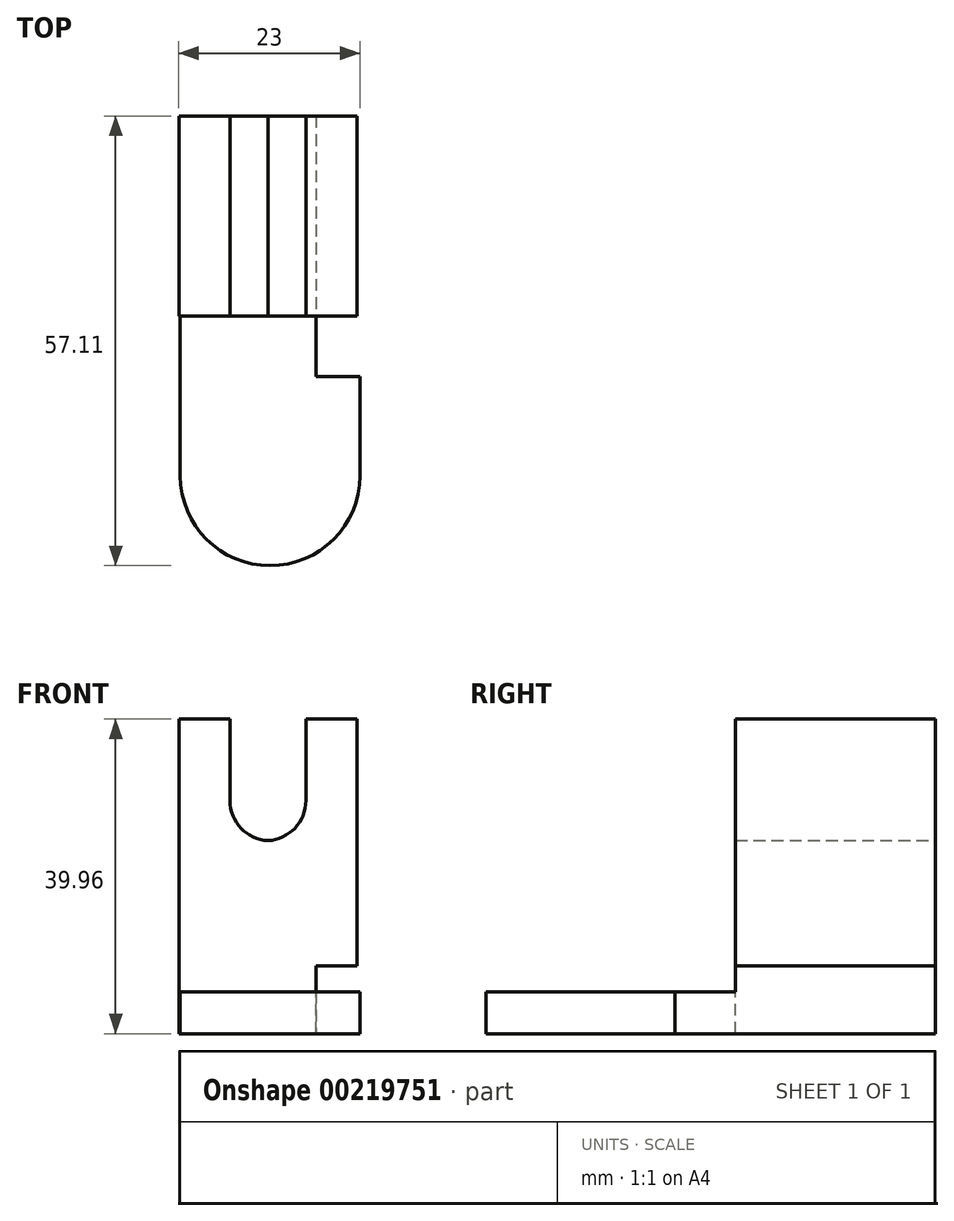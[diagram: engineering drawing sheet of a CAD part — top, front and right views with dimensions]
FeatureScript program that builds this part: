
annotation { "Feature Type Name" : "Feature", "Feature Type Description" : "" }
export const myFeature = defineFeature(function(context is Context, id is Id, definition is map)
    precondition{}
    {
        {
            var Q0;
            Q0=qCreatedBy(makeId("Front.planeOp"),FACE);
            var sketch = newSketch(context, id + "F0", { "sketchPlane" : qUnion([Q0])});
            skLineSegment(sketch, "E0.bottom", {"start": v(-11.13, 0) * mm, "end": v(11.5, 0) * mm});
            skLineSegment(sketch, "E0.top", {"start": v(-11.13, 39.96) * mm, "end": v(11.5, 39.96) * mm});
            skLineSegment(sketch, "E0.left", {"start": v(-11.13, 0) * mm, "end": v(-11.13, 39.96) * mm});
            skLineSegment(sketch, "E0.right", {"start": v(11.5, 0) * mm, "end": v(11.5, 39.96) * mm});
            skSolve(sketch);
        }
        {
            var Q0;
            Q0 = qSketchRegion(id + "F0", true);
            extrude(context, id + "F1", {"entities" : qUnion([Q0]), "depth" : 25.4 * mm});
        }
        {
            var Q0;
            Q0=makeQuery(id+"F1.opExtrude","CAP_FACE",FACE,{"disambiguationData":[OSD([sQuery(id+"F0.wireOp",EDGE,"E0.bottom"),sQuery(id+"F0.wireOp",EDGE,"E0.top"),sQuery(id+"F0.wireOp",EDGE,"E0.left"),sQuery(id+"F0.wireOp",EDGE,"E0.right")])],"isStart":false});
            var sketch = newSketch(context, id + "F2", { "sketchPlane" : qUnion([Q0])});
            skLineSegment(sketch, "E1.bottom", {"start": v(-4.64, 39.96) * mm, "end": v(5, 39.96) * mm});
            skLineSegment(sketch, "E1.top", {"start": v(-4.64, 24.52) * mm, "end": v(5, 24.52) * mm});
            skLineSegment(sketch, "E1.left", {"start": v(-4.64, 39.96) * mm, "end": v(-4.64, 24.52) * mm});
            skLineSegment(sketch, "E1.right", {"start": v(5, 39.96) * mm, "end": v(5, 24.52) * mm});
            skSolve(sketch);
        }
        {
            var Q0;
            Q0 = qSketchRegion(id + "F2", true);
            extrude(context, id + "F3", {"entities" : qUnion([Q0]), "operationType" : NewBodyOperationType.REMOVE, "endBound" : BoundingType.THROUGH_ALL, "oppositeDirection" : true, "depth" : 25.4 * mm});
        }
        {
            var Q0;
            Q0=makeQuery(id+"F3.boolean.opBoolean","COPY",EDGE,{"derivedFrom":makeQuery(id+"F3.opExtrude","SWEPT_EDGE",EDGE,{"disambiguationData":[OSD([sQuery(id+"F2.wireOp",EDGE,"E1.top"),sQuery(id+"F2.wireOp",EDGE,"E1.left")])]})});
            var Q1;
            Q1=makeQuery(id+"F3.boolean.opBoolean","COPY",EDGE,{"derivedFrom":makeQuery(id+"F3.opExtrude","SWEPT_EDGE",EDGE,{"disambiguationData":[OSD([sQuery(id+"F2.wireOp",EDGE,"E1.top"),sQuery(id+"F2.wireOp",EDGE,"E1.right")])]})});
            fillet(context, id + "F4", {"entities" : qUnion([Q0, Q1]), "radius" : 5.08 * mm, "tangentPropagation" : true, "allowEdgeOverflow" : false});
        }
        {
            var Q0;
            Q0=makeQuery(id+"F1.opExtrude","CAP_FACE",FACE,{"disambiguationData":[OSD([sQuery(id+"F0.wireOp",EDGE,"E0.bottom"),sQuery(id+"F0.wireOp",EDGE,"E0.top"),sQuery(id+"F0.wireOp",EDGE,"E0.left"),sQuery(id+"F0.wireOp",EDGE,"E0.right")])],"isStart":false});
            var sketch = newSketch(context, id + "F5", { "sketchPlane" : qUnion([Q0])});
            skLineSegment(sketch, "E2.bottom", {"start": v(11.5, 0) * mm, "end": v(6.3, 0) * mm});
            skLineSegment(sketch, "E2.top", {"start": v(11.5, 8.62) * mm, "end": v(6.3, 8.62) * mm});
            skLineSegment(sketch, "E2.left", {"start": v(11.5, 0) * mm, "end": v(11.5, 8.62) * mm});
            skLineSegment(sketch, "E2.right", {"start": v(6.3, 0) * mm, "end": v(6.3, 8.62) * mm});
            skSolve(sketch);
        }
        {
            var Q0;
            Q0=makeQuery(id+"F5.imprint","IMPRINT",FACE,{"disambiguationData":[TD([[makeQuery(id+"F5.imprint","IMPRINT",EDGE,{"derivedFrom":sQuery(id+"F5.wireOp",EDGE,"E2.bottom")}),1.0]])]});
            extrude(context, id + "F6", {"entities" : qUnion([Q0]), "operationType" : NewBodyOperationType.REMOVE, "endBound" : BoundingType.THROUGH_ALL, "oppositeDirection" : true, "depth" : 25.4 * mm});
        }
        {
            var Q0;
            Q0=qCreatedBy(makeId("Top.planeOp"),FACE);
            var sketch = newSketch(context, id + "F7", { "sketchPlane" : qUnion([Q0])});
            skLineSegment(sketch, "E3.bottom", {"start": v(-10.94, 0) * mm, "end": v(6.3, 0) * mm});
            skLineSegment(sketch, "E3.left", {"start": v(-10.94, 0) * mm, "end": v(-10.94, -45.7) * mm});
            skLineSegment(sketch, "E3.right", {"start": v(11.87, -33.1) * mm, "end": v(11.87, -45.7) * mm});
            skLineSegment(sketch, "E4.0", {"start": v(6.3, 0) * mm, "end": v(6.3, -25.4) * mm});
            skLineSegment(sketch, "E5", {"start": v(6.3, -25.4) * mm, "end": v(6.3, -33.1) * mm});
            skLineSegment(sketch, "E6", {"start": v(6.3, -33.1) * mm, "end": v(11.87, -33.1) * mm});
            skArc(sketch, "E7", {"start": v(-10.94, -45.7) * mm, "mid": v(0.46, -57.11) * mm, "end": v(11.87, -45.7) * mm});
            skSolve(sketch);
        }
        {
            var Q0;
            Q0 = qSketchRegion(id + "F7", true);
            extrude(context, id + "F8", {"entities" : qUnion([Q0]), "operationType" : NewBodyOperationType.ADD, "depth" : 0.25 * mm});
        }
        {
            var Q0;
            Q0=makeQuery(id+"F8.opExtrude","CAP_FACE",FACE,{"disambiguationData":[OSD([sQuery(id+"F7.wireOp",EDGE,"E3.bottom"),sQuery(id+"F7.wireOp",EDGE,"E3.top"),sQuery(id+"F7.wireOp",EDGE,"E3.left"),sQuery(id+"F7.wireOp",EDGE,"E3.right")])],"isStart":false});
            extrude(context, id + "F9", {"entities" : qUnion([Q0]), "operationType" : NewBodyOperationType.ADD, "depth" : 5.08 * mm});
        }
    });
